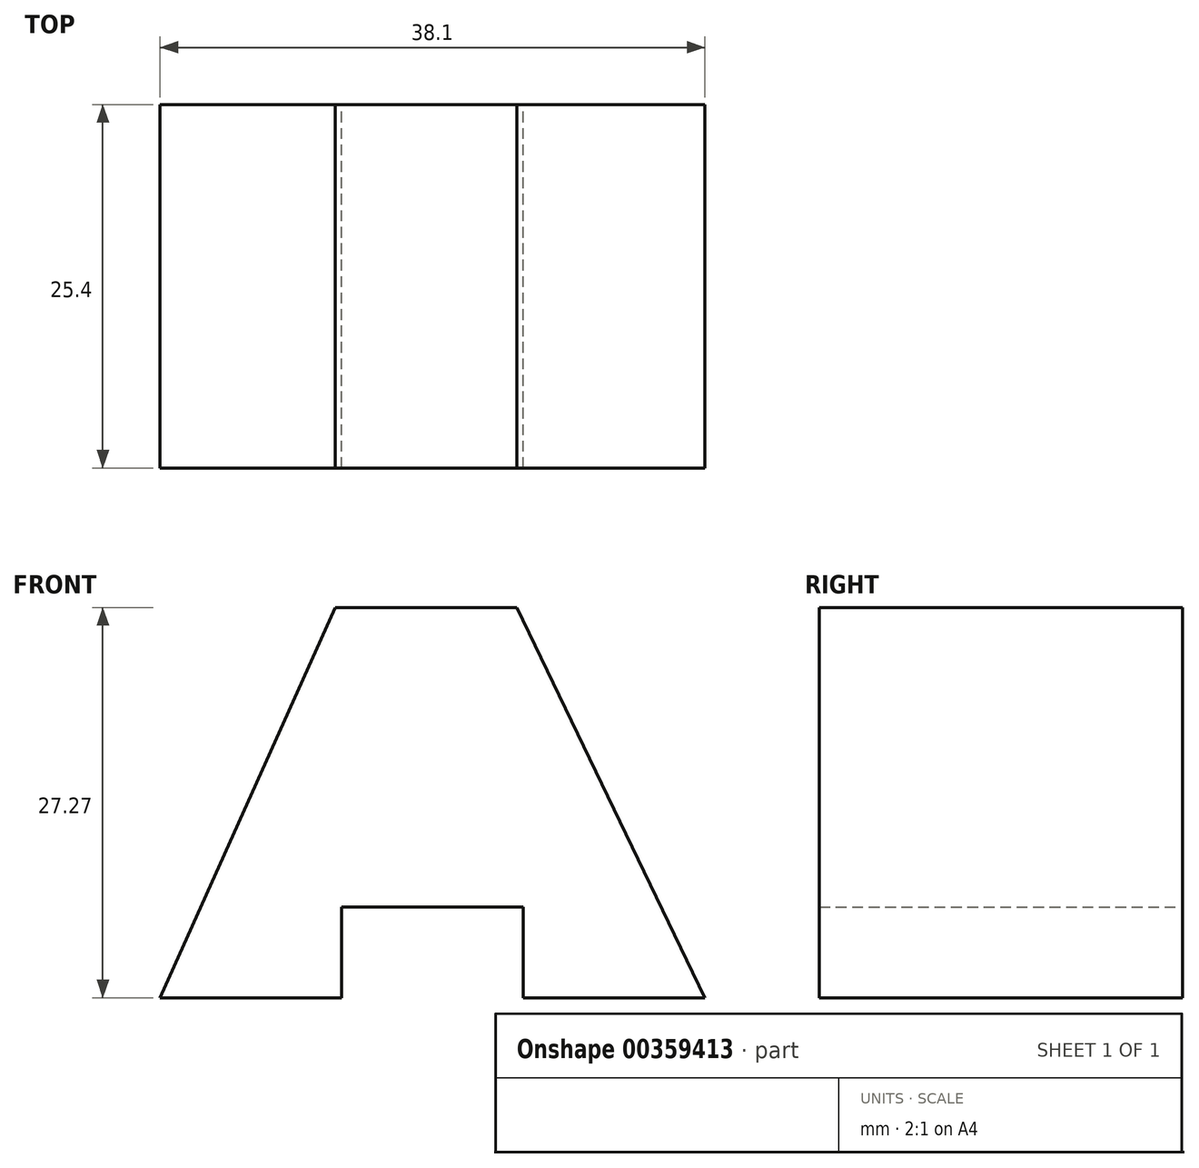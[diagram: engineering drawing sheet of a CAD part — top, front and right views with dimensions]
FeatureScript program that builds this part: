
annotation { "Feature Type Name" : "Feature", "Feature Type Description" : "" }
export const myFeature = defineFeature(function(context is Context, id is Id, definition is map)
    precondition{}
    {
        {
            var Q0;
            Q0=qCreatedBy(makeId("Front.planeOp"),FACE);
            var sketch = newSketch(context, id + "F0", { "sketchPlane" : qUnion([Q0])});
            skLineSegment(sketch, "E0", {"start": v(23.9, 27.27) * mm, "end": v(36.6, 27.27) * mm});
            skLineSegment(sketch, "E1", {"start": v(36.6, 27.27) * mm, "end": v(49.77, 0) * mm});
            skLineSegment(sketch, "E2", {"start": v(49.77, 0) * mm, "end": v(37.07, 0) * mm});
            skLineSegment(sketch, "E3", {"start": v(37.07, 0) * mm, "end": v(37.07, 6.35) * mm});
            skLineSegment(sketch, "E4", {"start": v(37.07, 6.35) * mm, "end": v(24.37, 6.35) * mm});
            skLineSegment(sketch, "E5", {"start": v(24.37, 6.35) * mm, "end": v(24.37, 0) * mm});
            skLineSegment(sketch, "E6", {"start": v(24.37, 0) * mm, "end": v(11.67, 0) * mm});
            skLineSegment(sketch, "E7", {"start": v(11.67, 0) * mm, "end": v(23.9, 27.27) * mm});
            skSolve(sketch);
        }
        {
            var Q0;
            Q0=makeQuery(id+"F0.imprint","IMPRINT",FACE,{"disambiguationData":[TD([[makeQuery(id+"F0.imprint","IMPRINT",EDGE,{"derivedFrom":sQuery(id+"F0.wireOp",EDGE,"E0")}),-1.0]])]});
            extrude(context, id + "F1", {"entities" : qUnion([Q0]), "depth" : 25.4 * mm});
        }
    });
